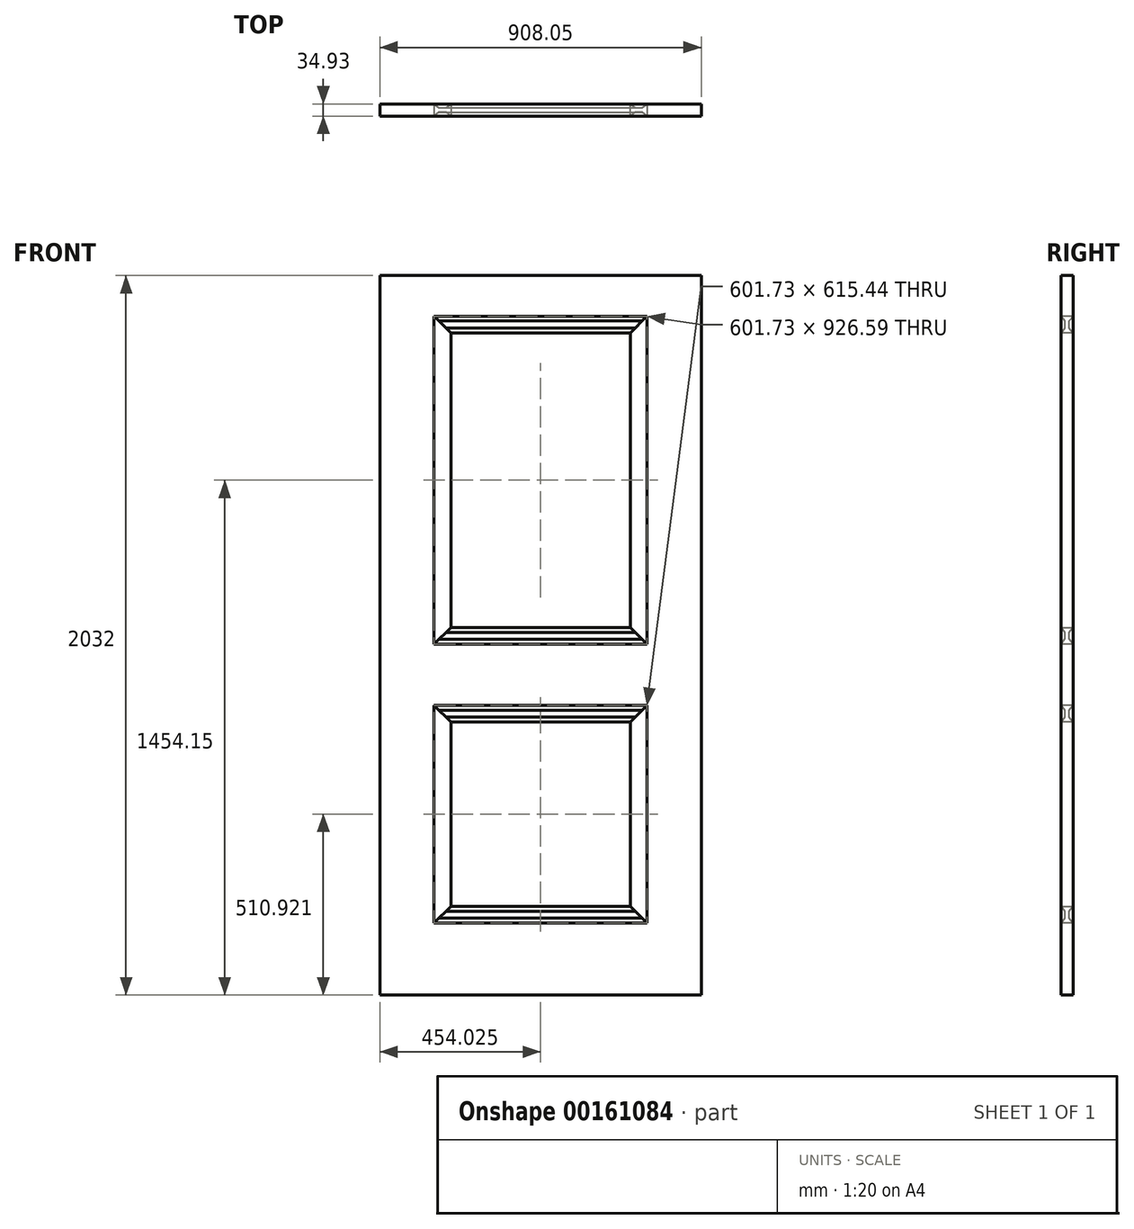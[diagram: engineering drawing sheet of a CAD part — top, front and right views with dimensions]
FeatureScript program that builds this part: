
annotation { "Feature Type Name" : "Feature", "Feature Type Description" : "" }
export const myFeature = defineFeature(function(context is Context, id is Id, definition is map)
    precondition{}
    {
        {
            var Q0;
            Q0=qCreatedBy(makeId("Top.planeOp"),FACE);
            var sketch = newSketch(context, id + "F0", { "sketchPlane" : qUnion([Q0])});
            skLineSegment(sketch, "E0.bottom", {"start": v(0, 0) * mm, "end": v(-908.05, 0) * mm});
            skLineSegment(sketch, "E0.top", {"start": v(0, 34.93) * mm, "end": v(-908.05, 34.93) * mm});
            skLineSegment(sketch, "E0.left", {"start": v(0, 0) * mm, "end": v(0, 34.93) * mm});
            skLineSegment(sketch, "E0.right", {"start": v(-908.05, 0) * mm, "end": v(-908.05, 34.93) * mm});
            skSolve(sketch);
        }
        {
            var Q0;
            Q0=qSketchRegion(id+"F0",true);
            extrude(context, id + "F1", {"entities" : qUnion([Q0]), "depth" : 2032 * mm});
        }
        {
            var Q0;
            Q0=qCreatedBy(makeId("Front.planeOp"),FACE);
            var sketch = newSketch(context, id + "F2", { "sketchPlane" : qUnion([Q0])});
            skLineSegment(sketch, "E1.top", {"start": v(-754.89, 990.85) * mm, "end": v(-153.16, 990.85) * mm});
            skLineSegment(sketch, "E1.left", {"start": v(-754.89, 1917.45) * mm, "end": v(-754.89, 990.85) * mm});
            skLineSegment(sketch, "E1.right", {"start": v(-153.16, 1917.45) * mm, "end": v(-153.16, 990.85) * mm});
            skLineSegment(sketch, "E2", {"start": v(-754.89, 1917.45) * mm, "end": v(-454.02, 1917.45) * mm});
            skLineSegment(sketch, "E3", {"start": v(-454.02, 1917.45) * mm, "end": v(-153.16, 1917.45) * mm});
            skPoint(sketch, "E4.0", {"position": v(-454.03, 2032) * mm});
            skLineSegment(sketch, "E5.bottom", {"start": v(-754.89, 818.64) * mm, "end": v(-153.16, 818.64) * mm});
            skLineSegment(sketch, "E5.top", {"start": v(-754.89, 203.2) * mm, "end": v(-153.16, 203.2) * mm});
            skLineSegment(sketch, "E5.left", {"start": v(-754.89, 818.64) * mm, "end": v(-754.89, 203.2) * mm});
            skLineSegment(sketch, "E5.right", {"start": v(-153.16, 818.64) * mm, "end": v(-153.16, 203.2) * mm});
            skSolve(sketch);
        }
        {
            var Q0;
            Q0=qSketchRegion(id+"F2",true);
            extrude(context, id + "F3", {"entities" : qUnion([Q0]), "operationType" : NewBodyOperationType.REMOVE, "endBound" : BoundingType.THROUGH_ALL, "oppositeDirection" : true, "depth" : 25.4 * mm});
        }
        {
            var Q0;
            Q0=qCreatedBy(makeId("Top.planeOp"),FACE);
            var sketch = newSketch(context, id + "F4", { "sketchPlane" : qUnion([Q0])});
            skPoint(sketch, "E6.0", {"position": v(-153.16, 17.46) * mm});
            skPoint(sketch, "E7.0", {"position": v(-153.16, 34.93) * mm});
            skLineSegment(sketch, "E8", {"start": v(-153.16, 17.46) * mm, "end": v(-153.16, 34.93) * mm});
            skLineSegment(sketch, "E9", {"start": v(-153.16, 34.93) * mm, "end": v(-167, 24) * mm});
            skLineSegment(sketch, "E10", {"start": v(-167, 24) * mm, "end": v(-176.91, 24) * mm});
            skLineSegment(sketch, "E11", {"start": v(-176.91, 24) * mm, "end": v(-176.91, 59.2) * mm, "construction": true});
            skLineSegment(sketch, "E12", {"start": v(-153.16, 17.46) * mm, "end": v(-138.76, 17.46) * mm, "construction": true});
            skLineSegment(sketch, "E13.MirrorCS", {"start": v(-186.81, 24) * mm, "end": v(-176.91, 24) * mm});
            skLineSegment(sketch, "E14.MirrorCS", {"start": v(-200.66, 34.93) * mm, "end": v(-186.81, 24) * mm});
            skLineSegment(sketch, "E15.MirrorCS", {"start": v(-200.66, 17.46) * mm, "end": v(-200.66, 34.93) * mm});
            skLineSegment(sketch, "E16.MirrorCS", {"start": v(-153.16, 17.46) * mm, "end": v(-153.16, 0) * mm});
            skLineSegment(sketch, "E17.MirrorCS", {"start": v(-153.16, 0) * mm, "end": v(-167, 10.92) * mm});
            skLineSegment(sketch, "E18.MirrorCS", {"start": v(-167, 10.92) * mm, "end": v(-176.91, 10.92) * mm});
            skLineSegment(sketch, "E19.MirrorCS", {"start": v(-186.81, 10.92) * mm, "end": v(-176.91, 10.92) * mm});
            skLineSegment(sketch, "E20.MirrorCS", {"start": v(-200.66, 0) * mm, "end": v(-186.81, 10.92) * mm});
            skLineSegment(sketch, "E21.MirrorCS", {"start": v(-200.66, 17.46) * mm, "end": v(-200.66, 0) * mm});
            skLineSegment(sketch, "E22", {"start": v(-153.16, -1072) * mm, "end": v(-754.89, -1072) * mm, "construction": true});
            skLineSegment(sketch, "E23", {"start": v(-454.03, -1072) * mm, "end": v(-454.03, -1072) * mm});
            skPoint(sketch, "E23.endSnap0", {"position": v(-454.03, -1072) * mm});
            skPoint(sketch, "E24.0", {"position": v(-754.89, 34.92) * mm});
            skLineSegment(sketch, "E25", {"start": v(-754.89, 96.95) * mm, "end": v(-153.16, 96.95) * mm, "construction": true});
            skLineSegment(sketch, "E26", {"start": v(-454.03, 96.95) * mm, "end": v(-454.03, 139.27) * mm, "construction": true});
            skLineSegment(sketch, "E27.MirrorCS", {"start": v(-754.89, 17.46) * mm, "end": v(-754.89, 34.92) * mm});
            skLineSegment(sketch, "E28.MirrorCS", {"start": v(-754.89, 17.46) * mm, "end": v(-754.89, 0) * mm});
            skLineSegment(sketch, "E29.MirrorCS", {"start": v(-754.89, 0) * mm, "end": v(-741.04, 10.92) * mm});
            skLineSegment(sketch, "E30.MirrorCS", {"start": v(-741.04, 10.92) * mm, "end": v(-731.14, 10.92) * mm});
            skLineSegment(sketch, "E31.MirrorCS", {"start": v(-721.24, 10.92) * mm, "end": v(-731.14, 10.92) * mm});
            skLineSegment(sketch, "E32.MirrorCS", {"start": v(-707.4, 0) * mm, "end": v(-721.24, 10.92) * mm});
            skLineSegment(sketch, "E33.MirrorCS", {"start": v(-707.4, 17.46) * mm, "end": v(-707.4, 0) * mm});
            skLineSegment(sketch, "E34.MirrorCS", {"start": v(-707.4, 17.46) * mm, "end": v(-707.4, 34.93) * mm});
            skLineSegment(sketch, "E35.MirrorCS", {"start": v(-707.4, 34.93) * mm, "end": v(-721.24, 24) * mm});
            skLineSegment(sketch, "E36.MirrorCS", {"start": v(-721.24, 24) * mm, "end": v(-731.14, 24) * mm});
            skLineSegment(sketch, "E37.MirrorCS", {"start": v(-741.04, 24) * mm, "end": v(-731.14, 24) * mm});
            skLineSegment(sketch, "E38.MirrorCS", {"start": v(-754.89, 34.93) * mm, "end": v(-741.04, 24) * mm});
            skSolve(sketch);
        }
        {
            var Q0;
            Q0=qCreatedBy(makeId("Front.planeOp"),FACE);
            var sketch = newSketch(context, id + "F5", { "sketchPlane" : qUnion([Q0])});
            skPoint(sketch, "E39.0", {"position": v(-754.89, 1917.45) * mm});
            skPoint(sketch, "E40.0", {"position": v(-153.16, 1917.45) * mm});
            skPoint(sketch, "E41.0", {"position": v(-153.16, 990.85) * mm});
            skPoint(sketch, "E42.0", {"position": v(-754.89, 990.85) * mm});
            skPoint(sketch, "E43.0", {"position": v(-754.89, 818.64) * mm});
            skPoint(sketch, "E44.0", {"position": v(-153.16, 818.64) * mm});
            skPoint(sketch, "E45.0", {"position": v(-754.89, 203.2) * mm});
            skPoint(sketch, "E46.0", {"position": v(-153.16, 203.2) * mm});
            skLineSegment(sketch, "E47", {"start": v(-754.89, 1917.45) * mm, "end": v(-454.02, 1616.58) * mm});
            skLineSegment(sketch, "E48", {"start": v(-454.02, 1616.58) * mm, "end": v(-153.16, 1917.45) * mm});
            skLineSegment(sketch, "E49", {"start": v(-754.89, 818.64) * mm, "end": v(-454.02, 517.78) * mm});
            skLineSegment(sketch, "E50", {"start": v(-454.02, 517.78) * mm, "end": v(-153.16, 818.64) * mm});
            skLineSegment(sketch, "E51", {"start": v(-754.89, 1917.45) * mm, "end": v(-869.44, 2032) * mm});
            skLineSegment(sketch, "E52", {"start": v(-869.44, 2032) * mm, "end": v(-38.6, 2032) * mm});
            skLineSegment(sketch, "E53", {"start": v(-38.6, 2032) * mm, "end": v(-153.16, 1917.45) * mm});
            skLineSegment(sketch, "E54", {"start": v(-754.89, 818.64) * mm, "end": v(-1968.25, 2032) * mm});
            skLineSegment(sketch, "E55", {"start": v(-1968.25, 2032) * mm, "end": v(1060.2, 2032) * mm});
            skLineSegment(sketch, "E56", {"start": v(1060.2, 2032) * mm, "end": v(-153.16, 818.64) * mm});
            skLineSegment(sketch, "E57", {"start": v(-754.89, 990.85) * mm, "end": v(-454.03, 1291.72) * mm});
            skLineSegment(sketch, "E58", {"start": v(-454.02, 1291.72) * mm, "end": v(-153.16, 990.85) * mm});
            skLineSegment(sketch, "E59", {"start": v(-754.89, 203.2) * mm, "end": v(-454.02, 504.06) * mm});
            skLineSegment(sketch, "E60", {"start": v(-454.02, 504.06) * mm, "end": v(-153.16, 203.2) * mm});
            skLineSegment(sketch, "E61", {"start": v(-754.89, 990.85) * mm, "end": v(-1745.74, 0) * mm});
            skLineSegment(sketch, "E62", {"start": v(-1745.74, 0) * mm, "end": v(837.7, 0) * mm});
            skLineSegment(sketch, "E63", {"start": v(837.7, 0) * mm, "end": v(-153.16, 990.85) * mm});
            skLineSegment(sketch, "E64", {"start": v(-153.16, 203.2) * mm, "end": v(50.04, 0) * mm});
            skLineSegment(sketch, "E65", {"start": v(50.04, 0) * mm, "end": v(-958.09, 0) * mm});
            skLineSegment(sketch, "E66", {"start": v(-958.09, 0) * mm, "end": v(-754.89, 203.2) * mm});
            skSolve(sketch);
        }
        {
            var Q0;
            Q0=makeQuery(id+"F3.boolean.opBoolean","COPY",FACE,{"derivedFrom":makeQuery(id+"F3.opExtrude","SWEPT_FACE",FACE,{"disambiguationData":[OSD([sQuery(id+"F2.wireOp",EDGE,"E2"),sQuery(id+"F2.wireOp",EDGE,"E3")])]})});
            var sketch = newSketch(context, id + "F6", { "sketchPlane" : qUnion([Q0])});
            skLineSegment(sketch, "E67.4", {"start": v(-200.66, -34.93) * mm, "end": v(-186.81, -24) * mm});
            skLineSegment(sketch, "E67.6", {"start": v(-200.66, -17.46) * mm, "end": v(-200.66, -34.93) * mm});
            skLineSegment(sketch, "E67.8", {"start": v(-200.66, 0) * mm, "end": v(-186.81, -10.92) * mm});
            skLineSegment(sketch, "E67.9", {"start": v(-200.66, -17.46) * mm, "end": v(-200.66, 0) * mm});
            skLineSegment(sketch, "E67.11", {"start": v(-153.16, -34.93) * mm, "end": v(-167, -24) * mm});
            skLineSegment(sketch, "E67.14", {"start": v(-186.81, -24) * mm, "end": v(-176.91, -24) * mm});
            skLineSegment(sketch, "E67.16", {"start": v(-153.16, -17.46) * mm, "end": v(-153.16, 0) * mm});
            skLineSegment(sketch, "E67.17", {"start": v(-153.16, 0) * mm, "end": v(-167, -10.92) * mm});
            skLineSegment(sketch, "E67.18", {"start": v(-167, -10.92) * mm, "end": v(-176.91, -10.92) * mm});
            skLineSegment(sketch, "E67.19", {"start": v(-186.81, -10.92) * mm, "end": v(-176.91, -10.92) * mm});
            skLineSegment(sketch, "E67.25", {"start": v(-153.16, -17.46) * mm, "end": v(-153.16, -34.93) * mm});
            skLineSegment(sketch, "E67.26", {"start": v(-167, -24) * mm, "end": v(-176.91, -24) * mm});
            skLineSegment(sketch, "E68.0.0", {"start": v(-731.14, -24) * mm, "end": v(-741.04, -24) * mm});
            skLineSegment(sketch, "E68.0.1", {"start": v(-741.04, -24) * mm, "end": v(-754.89, -34.93) * mm});
            skLineSegment(sketch, "E68.0.2", {"start": v(-754.89, -34.93) * mm, "end": v(-754.89, -17.46) * mm});
            skLineSegment(sketch, "E68.0.3", {"start": v(-754.89, -17.46) * mm, "end": v(-754.89, 0) * mm});
            skLineSegment(sketch, "E68.0.4", {"start": v(-754.89, 0) * mm, "end": v(-741.04, -10.92) * mm});
            skLineSegment(sketch, "E68.0.5", {"start": v(-741.04, -10.92) * mm, "end": v(-731.14, -10.92) * mm});
            skLineSegment(sketch, "E68.0.6", {"start": v(-731.14, -10.92) * mm, "end": v(-721.24, -10.92) * mm});
            skLineSegment(sketch, "E68.0.7", {"start": v(-721.24, -10.92) * mm, "end": v(-707.4, 0) * mm});
            skLineSegment(sketch, "E68.0.8", {"start": v(-707.4, 0) * mm, "end": v(-707.4, -17.46) * mm});
            skLineSegment(sketch, "E68.0.9", {"start": v(-707.4, -17.46) * mm, "end": v(-707.4, -34.93) * mm});
            skLineSegment(sketch, "E68.0.10", {"start": v(-707.4, -34.93) * mm, "end": v(-721.24, -24) * mm});
            skLineSegment(sketch, "E68.0.11", {"start": v(-721.24, -24) * mm, "end": v(-731.14, -24) * mm});
            skSolve(sketch);
        }
        {
            var Q0;
            Q0=makeQuery(id+"F3.boolean.opBoolean","COPY",FACE,{"derivedFrom":makeQuery(id+"F3.opExtrude","SWEPT_FACE",FACE,{"disambiguationData":[OSD([sQuery(id+"F2.wireOp",EDGE,"E5.top")])]})});
            var sketch = newSketch(context, id + "F7", { "sketchPlane" : qUnion([Q0])});
            skLineSegment(sketch, "E69.0", {"start": v(-200.66, 17.46) * mm, "end": v(-200.66, 0) * mm});
            skLineSegment(sketch, "E69.1", {"start": v(-153.16, 17.46) * mm, "end": v(-153.16, 34.93) * mm});
            skLineSegment(sketch, "E69.2", {"start": v(-153.16, 34.93) * mm, "end": v(-167, 24) * mm});
            skLineSegment(sketch, "E69.3", {"start": v(-167, 24) * mm, "end": v(-176.91, 24) * mm});
            skLineSegment(sketch, "E69.4", {"start": v(-186.81, 24) * mm, "end": v(-176.91, 24) * mm});
            skLineSegment(sketch, "E69.5", {"start": v(-200.66, 34.93) * mm, "end": v(-186.81, 24) * mm});
            skLineSegment(sketch, "E69.6", {"start": v(-200.66, 17.46) * mm, "end": v(-200.66, 34.93) * mm});
            skLineSegment(sketch, "E69.7", {"start": v(-153.16, 17.46) * mm, "end": v(-153.16, 0) * mm});
            skLineSegment(sketch, "E69.8", {"start": v(-153.16, 0) * mm, "end": v(-167, 10.92) * mm});
            skLineSegment(sketch, "E69.9", {"start": v(-167, 10.92) * mm, "end": v(-176.91, 10.92) * mm});
            skLineSegment(sketch, "E69.10", {"start": v(-186.81, 10.92) * mm, "end": v(-176.91, 10.92) * mm});
            skLineSegment(sketch, "E69.11", {"start": v(-200.66, 0) * mm, "end": v(-186.81, 10.92) * mm});
            skLineSegment(sketch, "E70.0.0", {"start": v(-731.14, 24) * mm, "end": v(-741.04, 24) * mm});
            skLineSegment(sketch, "E70.0.1", {"start": v(-741.04, 24) * mm, "end": v(-754.89, 34.93) * mm});
            skLineSegment(sketch, "E70.0.2", {"start": v(-754.89, 34.93) * mm, "end": v(-754.89, 17.46) * mm});
            skLineSegment(sketch, "E70.0.3", {"start": v(-754.89, 17.46) * mm, "end": v(-754.89, 0) * mm});
            skLineSegment(sketch, "E70.0.4", {"start": v(-754.89, 0) * mm, "end": v(-741.04, 10.92) * mm});
            skLineSegment(sketch, "E70.0.5", {"start": v(-741.04, 10.92) * mm, "end": v(-731.14, 10.92) * mm});
            skLineSegment(sketch, "E70.0.6", {"start": v(-731.14, 10.92) * mm, "end": v(-721.24, 10.92) * mm});
            skLineSegment(sketch, "E70.0.7", {"start": v(-721.24, 10.92) * mm, "end": v(-707.4, 0) * mm});
            skLineSegment(sketch, "E70.0.8", {"start": v(-707.4, 0) * mm, "end": v(-707.4, 17.46) * mm});
            skLineSegment(sketch, "E70.0.9", {"start": v(-707.4, 17.46) * mm, "end": v(-707.4, 34.93) * mm});
            skLineSegment(sketch, "E70.0.10", {"start": v(-707.4, 34.93) * mm, "end": v(-721.24, 24) * mm});
            skLineSegment(sketch, "E70.0.11", {"start": v(-721.24, 24) * mm, "end": v(-731.14, 24) * mm});
            skSolve(sketch);
        }
        {
            var Q0;
            Q0=qSketchRegion(id+"F6",true);
            var Q1;
            Q1=makeQuery(id+"F3.boolean.opBoolean","COPY",FACE,{"derivedFrom":makeQuery(id+"F3.opExtrude","SWEPT_FACE",FACE,{"disambiguationData":[OSD([sQuery(id+"F2.wireOp",EDGE,"E1.top")])]})});
            extrude(context, id + "F8", {"entities" : qUnion([Q0]), "operationType" : NewBodyOperationType.ADD, "endBound" : BoundingType.UP_TO_SURFACE, "endBoundEntityFace" : qUnion([Q1]), "depth" : 307.34 * mm});
        }
        {
            var Q0;
            Q0=qSketchRegion(id+"F7",true);
            var Q1;
            Q1=makeQuery(id+"F3.boolean.opBoolean","COPY",FACE,{"derivedFrom":makeQuery(id+"F3.opExtrude","SWEPT_FACE",FACE,{"disambiguationData":[OSD([sQuery(id+"F2.wireOp",EDGE,"E5.bottom")])]})});
            extrude(context, id + "F9", {"entities" : qUnion([Q0]), "operationType" : NewBodyOperationType.ADD, "endBound" : BoundingType.UP_TO_SURFACE, "endBoundEntityFace" : qUnion([Q1]), "depth" : 25.4 * mm});
        }
        {
            var Q0;
            Q0=qCreatedBy(makeId("Front.planeOp"),FACE);
            var sketch = newSketch(context, id + "F10", { "sketchPlane" : qUnion([Q0])});
            skLineSegment(sketch, "E71.0", {"start": v(-454.02, 1616.58) * mm, "end": v(-153.16, 1917.45) * mm});
            skLineSegment(sketch, "E72.0", {"start": v(-754.89, 1917.45) * mm, "end": v(-454.02, 1616.58) * mm});
            skLineSegment(sketch, "E73.0", {"start": v(-200.66, 1917.45) * mm, "end": v(-153.16, 1917.45) * mm});
            skLineSegment(sketch, "E74.0", {"start": v(-454.02, 1291.72) * mm, "end": v(-153.16, 990.85) * mm});
            skLineSegment(sketch, "E75.0", {"start": v(-754.89, 990.85) * mm, "end": v(-454.03, 1291.72) * mm});
            skLineSegment(sketch, "E76.0", {"start": v(-200.66, 990.85) * mm, "end": v(-200.66, 990.85) * mm});
            skLineSegment(sketch, "E77.0", {"start": v(-200.66, 990.85) * mm, "end": v(-153.16, 990.85) * mm});
            skLineSegment(sketch, "E78.0", {"start": v(-754.89, 990.85) * mm, "end": v(-200.66, 990.85) * mm});
            skLineSegment(sketch, "E79.0", {"start": v(-200.66, 818.64) * mm, "end": v(-153.16, 818.64) * mm});
            skLineSegment(sketch, "E80.0", {"start": v(-454.02, 517.78) * mm, "end": v(-153.16, 818.64) * mm});
            skLineSegment(sketch, "E81.0", {"start": v(-754.89, 818.64) * mm, "end": v(-454.02, 517.78) * mm});
            skLineSegment(sketch, "E82.0", {"start": v(-200.66, 203.2) * mm, "end": v(-200.66, 203.2) * mm});
            skLineSegment(sketch, "E83.0", {"start": v(-200.66, 203.2) * mm, "end": v(-153.16, 203.2) * mm});
            skLineSegment(sketch, "E84.0", {"start": v(-754.89, 203.2) * mm, "end": v(-200.66, 203.2) * mm});
            skLineSegment(sketch, "E85.0", {"start": v(-754.89, 203.2) * mm, "end": v(-454.02, 504.06) * mm});
            skLineSegment(sketch, "E86.0", {"start": v(-454.02, 504.06) * mm, "end": v(-153.16, 203.2) * mm});
            skLineSegment(sketch, "E87.0", {"start": v(-754.89, 818.64) * mm, "end": v(-707.4, 818.64) * mm});
            skLineSegment(sketch, "E88.0", {"start": v(-707.4, 818.64) * mm, "end": v(-200.66, 818.64) * mm});
            skLineSegment(sketch, "E89.0", {"start": v(-754.89, 1917.45) * mm, "end": v(-707.4, 1917.45) * mm});
            skLineSegment(sketch, "E90.0", {"start": v(-707.4, 1917.45) * mm, "end": v(-200.66, 1917.45) * mm});
            skSolve(sketch);
        }
        {
            var Q0;
            Q0=qSketchRegion(id+"F10",true);
            extrude(context, id + "F11", {"entities" : qUnion([Q0]), "operationType" : NewBodyOperationType.REMOVE, "endBound" : BoundingType.THROUGH_ALL, "oppositeDirection" : true, "depth" : 25.4 * mm});
        }
        {
            var Q0;
            Q0=qCreatedBy(makeId("Right.planeOp"),FACE);
            var sketch = newSketch(context, id + "F12", { "sketchPlane" : qUnion([Q0])});
            skLineSegment(sketch, "E91.0.0", {"start": v(0, 1917.45) * mm, "end": v(34.92, 1917.45) * mm});
            skLineSegment(sketch, "E91.0.1", {"start": v(34.92, 1917.45) * mm, "end": v(24, 1903.6) * mm});
            skLineSegment(sketch, "E91.0.2", {"start": v(24, 1903.6) * mm, "end": v(24, 1883.8) * mm});
            skLineSegment(sketch, "E91.0.3", {"start": v(24, 1883.8) * mm, "end": v(34.92, 1869.95) * mm});
            skLineSegment(sketch, "E91.0.4", {"start": v(34.92, 1869.95) * mm, "end": v(0, 1869.95) * mm});
            skLineSegment(sketch, "E91.0.5", {"start": v(0, 1869.95) * mm, "end": v(10.92, 1883.8) * mm});
            skLineSegment(sketch, "E91.0.6", {"start": v(10.92, 1883.8) * mm, "end": v(10.92, 1903.6) * mm});
            skLineSegment(sketch, "E91.0.7", {"start": v(10.92, 1903.6) * mm, "end": v(0, 1917.45) * mm});
            skLineSegment(sketch, "E92.0.0", {"start": v(0, 990.85) * mm, "end": v(10.92, 1004.7) * mm});
            skLineSegment(sketch, "E92.0.1", {"start": v(10.92, 1004.7) * mm, "end": v(10.92, 1024.5) * mm});
            skLineSegment(sketch, "E92.0.2", {"start": v(10.92, 1024.5) * mm, "end": v(0, 1038.35) * mm});
            skLineSegment(sketch, "E92.0.3", {"start": v(0, 1038.35) * mm, "end": v(34.92, 1038.35) * mm});
            skLineSegment(sketch, "E92.0.4", {"start": v(34.93, 1038.35) * mm, "end": v(24, 1024.5) * mm});
            skLineSegment(sketch, "E92.0.5", {"start": v(24, 1024.5) * mm, "end": v(24, 1004.7) * mm});
            skLineSegment(sketch, "E92.0.6", {"start": v(24, 1004.7) * mm, "end": v(34.92, 990.85) * mm});
            skLineSegment(sketch, "E92.0.7", {"start": v(34.93, 990.85) * mm, "end": v(0, 990.85) * mm});
            skLineSegment(sketch, "E93.0.0", {"start": v(24, 804.8) * mm, "end": v(24, 784.99) * mm});
            skLineSegment(sketch, "E93.0.1", {"start": v(24, 784.99) * mm, "end": v(34.92, 771.14) * mm});
            skLineSegment(sketch, "E93.0.2", {"start": v(34.92, 771.14) * mm, "end": v(0, 771.14) * mm});
            skLineSegment(sketch, "E93.0.3", {"start": v(0, 771.14) * mm, "end": v(10.92, 784.99) * mm});
            skLineSegment(sketch, "E93.0.4", {"start": v(10.92, 784.99) * mm, "end": v(10.92, 804.8) * mm});
            skLineSegment(sketch, "E93.0.5", {"start": v(10.92, 804.8) * mm, "end": v(0, 818.64) * mm});
            skLineSegment(sketch, "E93.0.6", {"start": v(0, 818.64) * mm, "end": v(34.93, 818.64) * mm});
            skLineSegment(sketch, "E93.0.7", {"start": v(34.93, 818.64) * mm, "end": v(24, 804.8) * mm});
            skLineSegment(sketch, "E94.0.0", {"start": v(24, 217.05) * mm, "end": v(34.92, 203.2) * mm});
            skLineSegment(sketch, "E94.0.1", {"start": v(34.92, 203.2) * mm, "end": v(0, 203.2) * mm});
            skLineSegment(sketch, "E94.0.2", {"start": v(0, 203.2) * mm, "end": v(10.92, 217.05) * mm});
            skLineSegment(sketch, "E94.0.3", {"start": v(10.92, 217.05) * mm, "end": v(10.92, 236.85) * mm});
            skLineSegment(sketch, "E94.0.4", {"start": v(10.92, 236.85) * mm, "end": v(0, 250.7) * mm});
            skLineSegment(sketch, "E94.0.5", {"start": v(0, 250.7) * mm, "end": v(34.93, 250.7) * mm});
            skLineSegment(sketch, "E94.0.6", {"start": v(34.93, 250.7) * mm, "end": v(24, 236.85) * mm});
            skLineSegment(sketch, "E94.0.7", {"start": v(24, 236.85) * mm, "end": v(24, 217.05) * mm});
            skSolve(sketch);
        }
        {
            var Q0;
            Q0=qSketchRegion(id+"F12",true);
            var Q1;
            Q1=makeQuery(id+"F1.opExtrude","SWEPT_FACE",FACE,{"disambiguationData":[OSD([sQuery(id+"F0.wireOp",EDGE,"E0.right")])]});
            extrude(context, id + "F13", {"entities" : qUnion([Q0]), "endBound" : BoundingType.UP_TO_SURFACE, "oppositeDirection" : true, "endBoundEntityFace" : qUnion([Q1]), "depth" : 25.4 * mm});
        }
        {
            var Q0;
            Q0=qCreatedBy(makeId("Front.planeOp"),FACE);
            var sketch = newSketch(context, id + "F14", { "sketchPlane" : qUnion([Q0])});
            skLineSegment(sketch, "E95.0", {"start": v(-754.89, 203.2) * mm, "end": v(-454.02, 504.06) * mm});
            skLineSegment(sketch, "E96.0", {"start": v(-754.89, 818.64) * mm, "end": v(-454.02, 517.78) * mm});
            skLineSegment(sketch, "E97.0", {"start": v(-454.02, 504.06) * mm, "end": v(-153.16, 203.2) * mm});
            skLineSegment(sketch, "E98.0", {"start": v(-454.02, 517.78) * mm, "end": v(-153.16, 818.64) * mm});
            skLineSegment(sketch, "E99", {"start": v(-153.16, 818.64) * mm, "end": v(-153.16, 203.2) * mm});
            skLineSegment(sketch, "E100", {"start": v(-754.89, 818.64) * mm, "end": v(-754.89, 203.2) * mm});
            skLineSegment(sketch, "E101.0", {"start": v(-454.02, 1616.58) * mm, "end": v(-153.16, 1917.45) * mm});
            skLineSegment(sketch, "E102.0", {"start": v(-754.89, 1917.45) * mm, "end": v(-454.02, 1616.58) * mm});
            skLineSegment(sketch, "E103.0", {"start": v(-754.89, 990.85) * mm, "end": v(-454.03, 1291.72) * mm});
            skLineSegment(sketch, "E104.0", {"start": v(-454.02, 1291.72) * mm, "end": v(-153.16, 990.85) * mm});
            skLineSegment(sketch, "E105", {"start": v(-153.16, 1917.45) * mm, "end": v(-153.16, 990.85) * mm});
            skLineSegment(sketch, "E106", {"start": v(-754.89, 990.85) * mm, "end": v(-754.89, 1917.45) * mm});
            skSolve(sketch);
        }
        {
            var Q0;
            Q0=qSketchRegion(id+"F14",true);
            extrude(context, id + "F15", {"entities" : qUnion([Q0]), "operationType" : NewBodyOperationType.REMOVE, "endBound" : BoundingType.THROUGH_ALL, "oppositeDirection" : true, "depth" : 25.4 * mm});
        }
        {
            var Q0;
            Q0=makeQuery(id+"F1.opExtrude","SWEPT_BODY",BODY,{"disambiguationData":[OSD([sQuery(id+"F0.wireOp",EDGE,"E0.bottom"),sQuery(id+"F0.wireOp",EDGE,"E0.top"),sQuery(id+"F0.wireOp",EDGE,"E0.left"),sQuery(id+"F0.wireOp",EDGE,"E0.right")])]});
            var Q1;
            Q1=makeQuery(id+"F15.boolean.opBoolean","SPLIT",BODY,{"disambiguationData":[OD(0.0)],"derivedFrom":makeQuery(id+"F13.opExtrude","SWEPT_BODY",BODY,{"disambiguationData":[OSD([sQuery(id+"F12.wireOp",EDGE,"E91.0.0"),sQuery(id+"F12.wireOp",EDGE,"E91.0.1"),sQuery(id+"F12.wireOp",EDGE,"E91.0.2"),sQuery(id+"F12.wireOp",EDGE,"E91.0.3"),sQuery(id+"F12.wireOp",EDGE,"E91.0.4"),sQuery(id+"F12.wireOp",EDGE,"E91.0.5"),sQuery(id+"F12.wireOp",EDGE,"E91.0.6"),sQuery(id+"F12.wireOp",EDGE,"E91.0.7")])]})});
            var Q2;
            Q2=makeQuery(id+"F15.boolean.opBoolean","SPLIT",BODY,{"disambiguationData":[OD(1.0)],"derivedFrom":makeQuery(id+"F13.opExtrude","SWEPT_BODY",BODY,{"disambiguationData":[OSD([sQuery(id+"F12.wireOp",EDGE,"E91.0.0"),sQuery(id+"F12.wireOp",EDGE,"E91.0.1"),sQuery(id+"F12.wireOp",EDGE,"E91.0.2"),sQuery(id+"F12.wireOp",EDGE,"E91.0.3"),sQuery(id+"F12.wireOp",EDGE,"E91.0.4"),sQuery(id+"F12.wireOp",EDGE,"E91.0.5"),sQuery(id+"F12.wireOp",EDGE,"E91.0.6"),sQuery(id+"F12.wireOp",EDGE,"E91.0.7")])]})});
            var Q3;
            Q3=makeQuery(id+"F15.boolean.opBoolean","SPLIT",BODY,{"disambiguationData":[OD(2.0)],"derivedFrom":makeQuery(id+"F13.opExtrude","SWEPT_BODY",BODY,{"disambiguationData":[OSD([sQuery(id+"F12.wireOp",EDGE,"E91.0.0"),sQuery(id+"F12.wireOp",EDGE,"E91.0.1"),sQuery(id+"F12.wireOp",EDGE,"E91.0.2"),sQuery(id+"F12.wireOp",EDGE,"E91.0.3"),sQuery(id+"F12.wireOp",EDGE,"E91.0.4"),sQuery(id+"F12.wireOp",EDGE,"E91.0.5"),sQuery(id+"F12.wireOp",EDGE,"E91.0.6"),sQuery(id+"F12.wireOp",EDGE,"E91.0.7")])]})});
            var Q4;
            Q4=makeQuery(id+"F15.boolean.opBoolean","SPLIT",BODY,{"disambiguationData":[OD(0.0)],"derivedFrom":makeQuery(id+"F13.opExtrude","SWEPT_BODY",BODY,{"disambiguationData":[OSD([sQuery(id+"F12.wireOp",EDGE,"E92.0.0"),sQuery(id+"F12.wireOp",EDGE,"E92.0.1"),sQuery(id+"F12.wireOp",EDGE,"E92.0.2"),sQuery(id+"F12.wireOp",EDGE,"E92.0.3"),sQuery(id+"F12.wireOp",EDGE,"E92.0.4"),sQuery(id+"F12.wireOp",EDGE,"E92.0.5"),sQuery(id+"F12.wireOp",EDGE,"E92.0.6"),sQuery(id+"F12.wireOp",EDGE,"E92.0.7")])]})});
            var Q5;
            Q5=makeQuery(id+"F15.boolean.opBoolean","SPLIT",BODY,{"disambiguationData":[OD(1.0)],"derivedFrom":makeQuery(id+"F13.opExtrude","SWEPT_BODY",BODY,{"disambiguationData":[OSD([sQuery(id+"F12.wireOp",EDGE,"E92.0.0"),sQuery(id+"F12.wireOp",EDGE,"E92.0.1"),sQuery(id+"F12.wireOp",EDGE,"E92.0.2"),sQuery(id+"F12.wireOp",EDGE,"E92.0.3"),sQuery(id+"F12.wireOp",EDGE,"E92.0.4"),sQuery(id+"F12.wireOp",EDGE,"E92.0.5"),sQuery(id+"F12.wireOp",EDGE,"E92.0.6"),sQuery(id+"F12.wireOp",EDGE,"E92.0.7")])]})});
            var Q6;
            Q6=makeQuery(id+"F15.boolean.opBoolean","SPLIT",BODY,{"disambiguationData":[OD(2.0)],"derivedFrom":makeQuery(id+"F13.opExtrude","SWEPT_BODY",BODY,{"disambiguationData":[OSD([sQuery(id+"F12.wireOp",EDGE,"E92.0.0"),sQuery(id+"F12.wireOp",EDGE,"E92.0.1"),sQuery(id+"F12.wireOp",EDGE,"E92.0.2"),sQuery(id+"F12.wireOp",EDGE,"E92.0.3"),sQuery(id+"F12.wireOp",EDGE,"E92.0.4"),sQuery(id+"F12.wireOp",EDGE,"E92.0.5"),sQuery(id+"F12.wireOp",EDGE,"E92.0.6"),sQuery(id+"F12.wireOp",EDGE,"E92.0.7")])]})});
            var Q7;
            Q7=makeQuery(id+"F15.boolean.opBoolean","SPLIT",BODY,{"disambiguationData":[OD(0.0)],"derivedFrom":makeQuery(id+"F13.opExtrude","SWEPT_BODY",BODY,{"disambiguationData":[OSD([sQuery(id+"F12.wireOp",EDGE,"E93.0.0"),sQuery(id+"F12.wireOp",EDGE,"E93.0.1"),sQuery(id+"F12.wireOp",EDGE,"E93.0.2"),sQuery(id+"F12.wireOp",EDGE,"E93.0.3"),sQuery(id+"F12.wireOp",EDGE,"E93.0.4"),sQuery(id+"F12.wireOp",EDGE,"E93.0.5"),sQuery(id+"F12.wireOp",EDGE,"E93.0.6"),sQuery(id+"F12.wireOp",EDGE,"E93.0.7")])]})});
            var Q8;
            Q8=makeQuery(id+"F15.boolean.opBoolean","SPLIT",BODY,{"disambiguationData":[OD(1.0)],"derivedFrom":makeQuery(id+"F13.opExtrude","SWEPT_BODY",BODY,{"disambiguationData":[OSD([sQuery(id+"F12.wireOp",EDGE,"E93.0.0"),sQuery(id+"F12.wireOp",EDGE,"E93.0.1"),sQuery(id+"F12.wireOp",EDGE,"E93.0.2"),sQuery(id+"F12.wireOp",EDGE,"E93.0.3"),sQuery(id+"F12.wireOp",EDGE,"E93.0.4"),sQuery(id+"F12.wireOp",EDGE,"E93.0.5"),sQuery(id+"F12.wireOp",EDGE,"E93.0.6"),sQuery(id+"F12.wireOp",EDGE,"E93.0.7")])]})});
            var Q9;
            Q9=makeQuery(id+"F15.boolean.opBoolean","SPLIT",BODY,{"disambiguationData":[OD(2.0)],"derivedFrom":makeQuery(id+"F13.opExtrude","SWEPT_BODY",BODY,{"disambiguationData":[OSD([sQuery(id+"F12.wireOp",EDGE,"E93.0.0"),sQuery(id+"F12.wireOp",EDGE,"E93.0.1"),sQuery(id+"F12.wireOp",EDGE,"E93.0.2"),sQuery(id+"F12.wireOp",EDGE,"E93.0.3"),sQuery(id+"F12.wireOp",EDGE,"E93.0.4"),sQuery(id+"F12.wireOp",EDGE,"E93.0.5"),sQuery(id+"F12.wireOp",EDGE,"E93.0.6"),sQuery(id+"F12.wireOp",EDGE,"E93.0.7")])]})});
            var Q10;
            Q10=makeQuery(id+"F15.boolean.opBoolean","SPLIT",BODY,{"disambiguationData":[OD(0.0)],"derivedFrom":makeQuery(id+"F13.opExtrude","SWEPT_BODY",BODY,{"disambiguationData":[OSD([sQuery(id+"F12.wireOp",EDGE,"E94.0.0"),sQuery(id+"F12.wireOp",EDGE,"E94.0.1"),sQuery(id+"F12.wireOp",EDGE,"E94.0.2"),sQuery(id+"F12.wireOp",EDGE,"E94.0.3"),sQuery(id+"F12.wireOp",EDGE,"E94.0.4"),sQuery(id+"F12.wireOp",EDGE,"E94.0.5"),sQuery(id+"F12.wireOp",EDGE,"E94.0.6"),sQuery(id+"F12.wireOp",EDGE,"E94.0.7")])]})});
            var Q11;
            Q11=makeQuery(id+"F15.boolean.opBoolean","SPLIT",BODY,{"disambiguationData":[OD(1.0)],"derivedFrom":makeQuery(id+"F13.opExtrude","SWEPT_BODY",BODY,{"disambiguationData":[OSD([sQuery(id+"F12.wireOp",EDGE,"E94.0.0"),sQuery(id+"F12.wireOp",EDGE,"E94.0.1"),sQuery(id+"F12.wireOp",EDGE,"E94.0.2"),sQuery(id+"F12.wireOp",EDGE,"E94.0.3"),sQuery(id+"F12.wireOp",EDGE,"E94.0.4"),sQuery(id+"F12.wireOp",EDGE,"E94.0.5"),sQuery(id+"F12.wireOp",EDGE,"E94.0.6"),sQuery(id+"F12.wireOp",EDGE,"E94.0.7")])]})});
            var Q12;
            Q12=makeQuery(id+"F15.boolean.opBoolean","SPLIT",BODY,{"disambiguationData":[OD(2.0)],"derivedFrom":makeQuery(id+"F13.opExtrude","SWEPT_BODY",BODY,{"disambiguationData":[OSD([sQuery(id+"F12.wireOp",EDGE,"E94.0.0"),sQuery(id+"F12.wireOp",EDGE,"E94.0.1"),sQuery(id+"F12.wireOp",EDGE,"E94.0.2"),sQuery(id+"F12.wireOp",EDGE,"E94.0.3"),sQuery(id+"F12.wireOp",EDGE,"E94.0.4"),sQuery(id+"F12.wireOp",EDGE,"E94.0.5"),sQuery(id+"F12.wireOp",EDGE,"E94.0.6"),sQuery(id+"F12.wireOp",EDGE,"E94.0.7")])]})});
            booleanBodies(context, id + "F16", {"operationType" : BooleanOperationType.UNION, "tools" : qUnion([Q0, Q1, Q2, Q3, Q4, Q5, Q6, Q7, Q8, Q9, Q10, Q11, Q12])});
        }
        {
            var Q0;
            Q0=makeQuery(id+"F15.boolean.opBoolean","SPLIT",FACE,{"disambiguationData":[TD([makeQuery(id+"F15.opExtrude","SWEPT_FACE",FACE,{"disambiguationData":[OSD([sQuery(id+"F14.wireOp",EDGE,"E103.0")])]})])],"derivedFrom":makeQuery(id+"F13.opExtrude","SWEPT_FACE",FACE,{"disambiguationData":[OSD([sQuery(id+"F12.wireOp",EDGE,"E92.0.3")])]})});
            var sketch = newSketch(context, id + "F17", { "sketchPlane" : qUnion([Q0])});
            skLineSegment(sketch, "E107.0.0", {"start": v(-200.66, 34.92) * mm, "end": v(-707.4, 34.92) * mm});
            skLineSegment(sketch, "E107.0.1", {"start": v(-707.4, 34.92) * mm, "end": v(-707.4, 0) * mm});
            skLineSegment(sketch, "E107.0.2", {"start": v(-707.4, 0) * mm, "end": v(-200.66, 0) * mm});
            skLineSegment(sketch, "E107.0.3", {"start": v(-200.66, 0) * mm, "end": v(-200.66, 34.92) * mm});
            skSolve(sketch);
        }
        {
            var Q0;
            Q0=qSketchRegion(id+"F17",true);
            var Q1;
            Q1=makeQuery(id+"F15.boolean.opBoolean","SPLIT",FACE,{"disambiguationData":[TD([makeQuery(id+"F15.opExtrude","SWEPT_FACE",FACE,{"disambiguationData":[OSD([sQuery(id+"F14.wireOp",EDGE,"E101.0")])]})])],"derivedFrom":makeQuery(id+"F13.opExtrude","SWEPT_FACE",FACE,{"disambiguationData":[OSD([sQuery(id+"F12.wireOp",EDGE,"E91.0.4")])]})});
            extrude(context, id + "F18", {"entities" : qUnion([Q0]), "operationType" : NewBodyOperationType.ADD, "endBound" : BoundingType.UP_TO_SURFACE, "endBoundEntityFace" : qUnion([Q1]), "depth" : 25.4 * mm});
        }
        {
            var Q0;
            {var subQ0=sQuery(id+"F14.wireOp",EDGE,"E95.0");Q0=makeQuery(id+"F15.boolean.opBoolean","SPLIT",FACE,{"disambiguationData":[TD([makeQuery(id+"F15.opExtrude","SWEPT_FACE",FACE,{"disambiguationData":[OSD([subQ0]),TDD([makeQuery(id+"F14.imprint","IMPRINT",EDGE,{"disambiguationData":[TD([[makeQuery(id+"F14.imprint","INTERSECT",VERTEX,{"derivedFrom":[subQ0,sQuery(id+"F14.wireOp",EDGE,"E100")]}),-1.0]])],"derivedFrom":subQ0})])]})])],"derivedFrom":makeQuery(id+"F13.opExtrude","SWEPT_FACE",FACE,{"disambiguationData":[OSD([sQuery(id+"F12.wireOp",EDGE,"E94.0.5")])]})});}
            var sketch = newSketch(context, id + "F19", { "sketchPlane" : qUnion([Q0])});
            skLineSegment(sketch, "E108.0.0", {"start": v(-707.4, 0) * mm, "end": v(-200.66, 0) * mm});
            skLineSegment(sketch, "E108.0.1", {"start": v(-200.66, 0) * mm, "end": v(-200.66, 34.93) * mm});
            skLineSegment(sketch, "E108.0.2", {"start": v(-200.66, 34.93) * mm, "end": v(-707.4, 34.93) * mm});
            skLineSegment(sketch, "E108.0.3", {"start": v(-707.4, 34.93) * mm, "end": v(-707.4, 0) * mm});
            skSolve(sketch);
        }
        {
            var Q0;
            Q0=qSketchRegion(id+"F19",true);
            var Q1;
            {var subQ0=sQuery(id+"F14.wireOp",EDGE,"E96.0");Q1=makeQuery(id+"F15.boolean.opBoolean","SPLIT",FACE,{"disambiguationData":[TD([makeQuery(id+"F15.opExtrude","SWEPT_FACE",FACE,{"disambiguationData":[OSD([subQ0]),TDD([makeQuery(id+"F14.imprint","IMPRINT",EDGE,{"disambiguationData":[TD([[makeQuery(id+"F14.imprint","INTERSECT",VERTEX,{"derivedFrom":[subQ0,sQuery(id+"F14.wireOp",EDGE,"E100")]}),-1.0]])],"derivedFrom":subQ0})])]})])],"derivedFrom":makeQuery(id+"F13.opExtrude","SWEPT_FACE",FACE,{"disambiguationData":[OSD([sQuery(id+"F12.wireOp",EDGE,"E93.0.2")])]})});}
            extrude(context, id + "F20", {"entities" : qUnion([Q0]), "operationType" : NewBodyOperationType.ADD, "endBound" : BoundingType.UP_TO_SURFACE, "endBoundEntityFace" : qUnion([Q1]), "depth" : 25.4 * mm});
        }
    });
